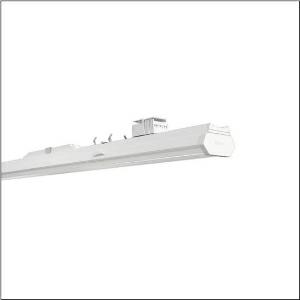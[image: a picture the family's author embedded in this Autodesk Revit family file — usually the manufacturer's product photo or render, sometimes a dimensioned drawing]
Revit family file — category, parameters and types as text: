
# Revit family: licross_r__21_protected_mo_52tp12dn4a5g3c_2390
name_source: partatom
category: Lighting Fixtures
units: mm (PartAtom-declared; Revit-internal decimal feet)

## family parameters
Cut with Voids When Loaded = No
Host = Face
Light Source = No
Part Type = Normal
Room Calculation Point = No
Round Connector Dimension = Use Diameter
Shared = No

## types (1)
- --- (1 x LED, 940 lm, 6.8 W, 4000K)
    Apparent Load = 7 VA
    CIE Flux Codes = 73 92 98 99 100
    Color Rendering = 80
    Color Temperature = 4000K
    Default Elevation = 1800 mm
    Description = Licross® 21 Protected MO, luminaire insert, of sheet steel, galvanised, coil coated, white, length: 1.500mm, width: 90mm, height: 103mm, LED rated luminous flux: 10.700lm, light colour: 840, control gear: DALI 2 (for two DALI lines), with plug, 6-pole, with phase selection, for trunking rail, 14-core, mains connection: 220..240V, AC, 50/60Hz, rated input power: 66W, for trunking rail, 14-core, halogen-free wiring, for emergency light function, converter,control gear: single battery element, battery: LiFePO4, 9Ah, primary light control with lens, of plastic, primary optical cover: cover, of PMMA, light emission: direct distribution, primary light characteristic: symmetric, protection rating (complete): IP64, insulation class (complete): insulation class I (protective earthing), certification: CE, UKCA, protection symbol: D if used in an environment with conductive dust loads with corresponding accessories, impact resistance: IK06, permissible ambient temperature for indoor applications: +5..+35°C, standard: EN 60598-2-22, LABS conformity tested according to VDMA 24364:2018-05, reducing of maximum allowable ambient temperature of 5°C with ceiling mounting, corresponds to IFS (International Featured Standards) requirements for safety and quality in the food industry, packaging unit: 1 piece
    Height = 92 mm
    Lamp = 1 x LED
    Lamp Light Flux = 940 lm
    Lamp Power = 6.8 W
    Lamp count = 1
    Length = 1500 mm
    Luminous efficacy = 138 lm/W
    Manufacturer = Siteco
    ModVariant = No
    Model = 52TP12DN4A5G3C
    Mounting Place = Ceiling
    Mounting Type = Pendant
    Number of Poles = 1
    OnlyDefault = Yes
    Power Factor = 1
    Product Name = Licross® 21 Protected MO
    Product group = luminaire insert
    ProductGroupID = 902
    Protection Class = Protection class I
    Protection Degree = IP 64
    RLX_Detail_Level = 1
    RLX_Emergency_Light_Flux = 0 lm
    RLX_Emergency_Type = 0
    RLX_Emergency_Type_DB = No
    RlxData = <blob elided: 24825 chars, md5=28cef660>
    Socket = socket
    Standby Power = 0 W
    System Light Flux = 940 lm
    System Power = 7 W
    Type Comments = : emergency light operation: 3 h
    Type Image = l_1256148.jpg
    URL = http://relux.com
    VarID = @adj_110930
    Voltage = 0 V
    Weight = 0.00 kg
    Width = 88 mm

## geometry (parser evidence)
native form markers: Blend x4, Sweep x10
no freeform markers — native parametric forms only
